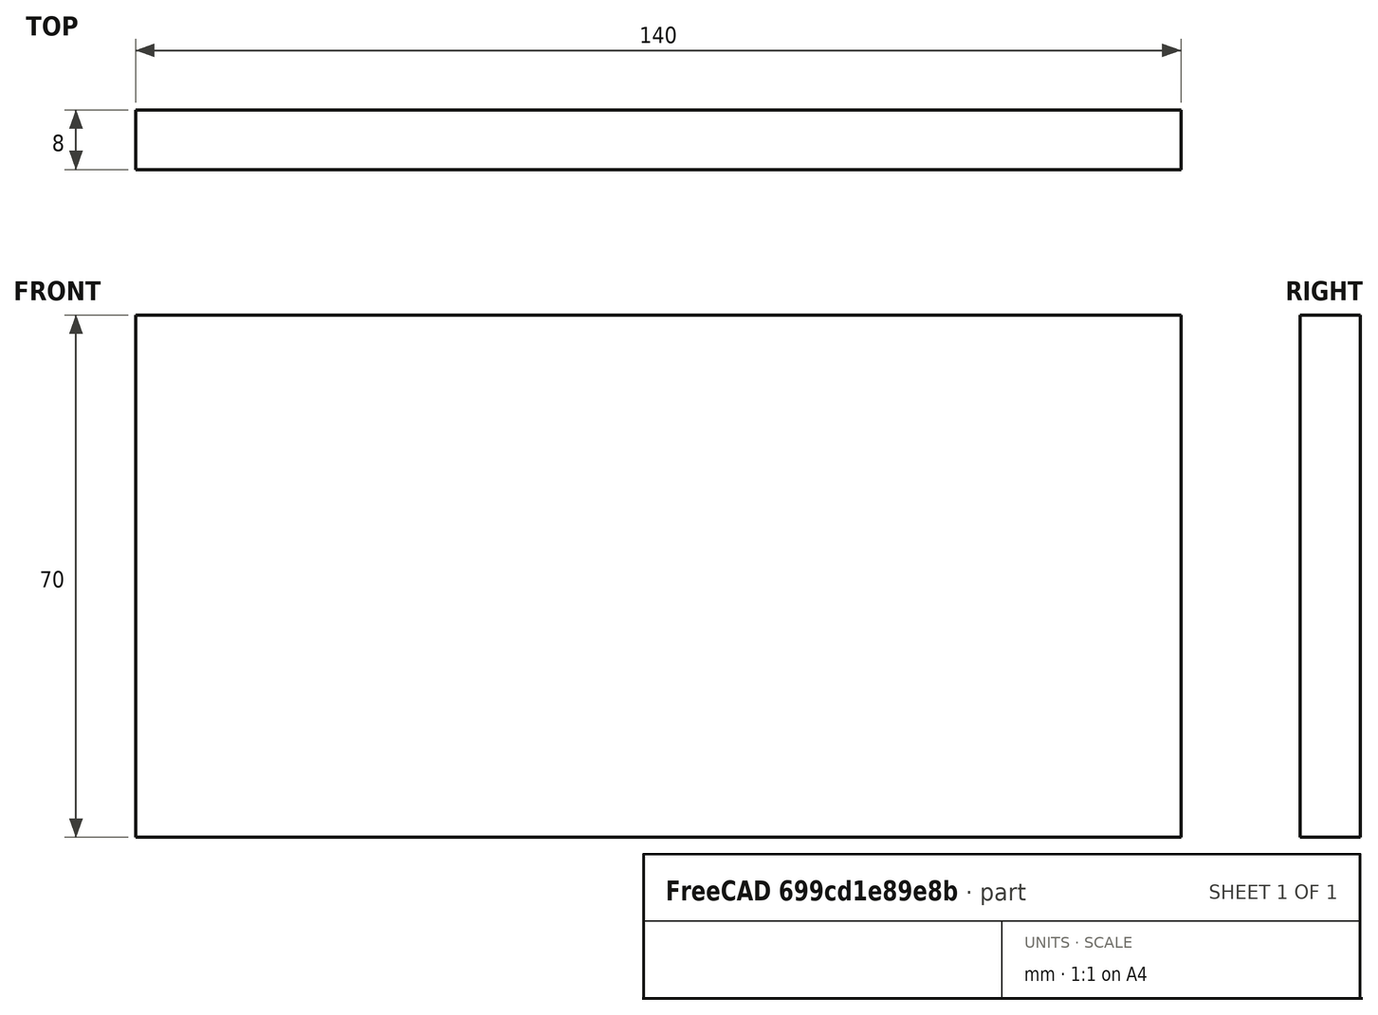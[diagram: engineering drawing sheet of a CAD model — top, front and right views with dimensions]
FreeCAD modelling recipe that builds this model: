
FCSTD DOCUMENT  (FreeCAD 2023.521R14555 (Git shallow))
Label: Back_spacer
License: All rights reserved
LicenseURL: https://en.wikipedia.org/wiki/All_rights_reserved
objects: Sketcher::SketchObject×1, PartDesign::Pad×1, PartDesign::Body×1
note: 6 computed .brp shape members not serialized (recipe doc carries the construction recipe); baked Part::Feature solids carry a one-line shape summary decoded from their .brp

FEATURE [Sketcher::SketchObject] Sketch
  ArcFitTolerance = 1e-06
  AttachmentSupport = -> [XZ_Plane]
  ExternalBSplineMaxDegree = 5
  ExternalBSplineTolerance = 0.0001
  FixShape = 1
  FullyConstrained = true
  InternalTolerance = 1e-06
  InvalidShape = false
  MakeInternals = false
  MapMode = 5
  Placement = pos=(0,0,0) rot=(1,0,0;1.5708rad)
  Support = -> [XZ_Plane]
  TreeRank = 11
  ValidateShape = false
  sketch-geometry (5):
    g0: LineSegment StartX=-70 StartY=-35 StartZ=0 EndX=-70 EndY=35 EndZ=0
    g1: LineSegment StartX=-70 StartY=35 StartZ=0 EndX=70 EndY=35 EndZ=0
    g2: LineSegment StartX=70 StartY=35 StartZ=0 EndX=70 EndY=-35 EndZ=0
    g3: LineSegment StartX=70 StartY=-35 StartZ=0 EndX=-70 EndY=-35 EndZ=0
    g4: GeomPoint [constr] X=0 Y=0 Z=0
  constraints (12):
    c: Coincident(g0,g1)
    c: Coincident(g1,g2)
    c: Coincident(g2,g3)
    c: Coincident(g3,g0)
    c: Horizontal(g1)
    c: Horizontal(g3)
    c: Vertical(g0)
    c: Vertical(g2)
    c: Symmetric(g1,g0,g4)
    c: Coincident(g4,g-1)
    c: DistanceX(g3,g3) = 140
    c: DistanceY(g2,g2) = 70
FEATURE [PartDesign::Pad] Pad
  AddSubType = 0
  AlongSketchNormal = false
  AutoTaperInnerAngle = true
  CheckUpToFaceLimits = true
  ClaimChildren = false
  Direction = (0,-1,2e-16)
  Fit = 0
  FitJoin = 0
  FixShape = 1
  InnerFit = 0
  InnerFitJoin = 0
  InvalidShape = false
  Length = 8
  Length2 = 10
  Linearize = true
  NewSolid = false
  Profile = -> Sketch
  ReferenceAxis = -> Sketch [N_Axis]
  Refine = true
  Suppress = false
  TaperInnerAngle = 0
  TaperInnerAngleRev = 0
  TreeRank = 12
  Type = 0
  ValidateShape = true
  _ProfileBasedVersion = 1
FEATURE [PartDesign::Body] Body
  AutoGroupSolids = false
  ClaimAllChildren = false
  ExportMode = 0
  FixShape = 1
  Group = -> [Sketch,Pad]
  InvalidShape = false
  Origin = -> Origin
  Tip = -> Pad
  TreeRank = 10
  ValidateShape = false
  _ExportChildren = -> [Pad]
  _GroupVersion = 1
